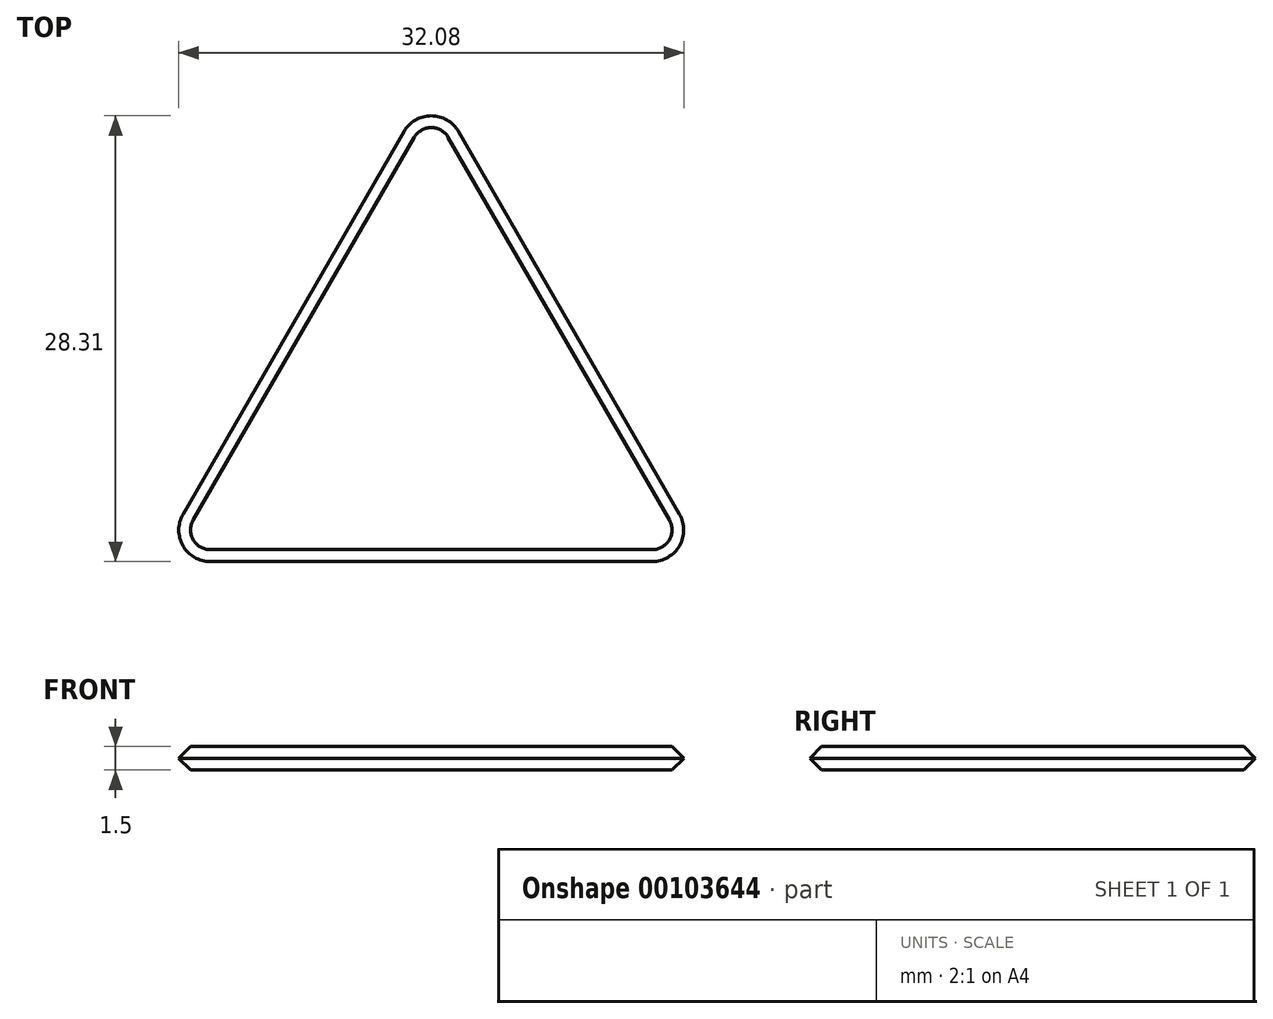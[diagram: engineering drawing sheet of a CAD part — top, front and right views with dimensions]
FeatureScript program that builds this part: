
annotation { "Feature Type Name" : "Feature", "Feature Type Description" : "" }
export const myFeature = defineFeature(function(context is Context, id is Id, definition is map)
    precondition{}
    {
        {
            var Q0;
            Q0=qCreatedBy(makeId("Top.planeOp"),FACE);
            var sketch = newSketch(context, id + "F0", { "sketchPlane" : qUnion([Q0])});
            skLineSegment(sketch, "E0", {"start": v(-1.73, 27.31) * mm, "end": v(-15.77, 3) * mm});
            skLineSegment(sketch, "E1", {"start": v(-14.04, 0) * mm, "end": v(14.04, 0) * mm});
            skLineSegment(sketch, "E2", {"start": v(15.77, 3) * mm, "end": v(1.73, 27.31) * mm});
            skPoint(sketch, "E3.visualSharp", {"position": v(0, 30.31) * mm});
            skArc(sketch, "E3.filletArc", {"start": v(1.73, 27.31) * mm, "mid": v(0, 28.31) * mm, "end": v(-1.73, 27.31) * mm});
            skPoint(sketch, "E4.visualSharp", {"position": v(17.5, 0) * mm});
            skArc(sketch, "E4.filletArc", {"start": v(14.04, 0) * mm, "mid": v(15.77, 1) * mm, "end": v(15.77, 3) * mm});
            skPoint(sketch, "E5.visualSharp", {"position": v(-17.5, 0) * mm});
            skArc(sketch, "E5.filletArc", {"start": v(-15.77, 3) * mm, "mid": v(-15.77, 1) * mm, "end": v(-14.04, 0) * mm});
            skSolve(sketch);
        }
        {
            var Q0;
            Q0=makeQuery(id+"F0.imprint","IMPRINT",FACE,{"disambiguationData":[TD([[makeQuery(id+"F0.imprint","IMPRINT",EDGE,{"derivedFrom":sQuery(id+"F0.wireOp",EDGE,"E0")}),1.0]])]});
            extrude(context, id + "F1", {"entities" : qUnion([Q0]), "endBound" : BoundingType.SYMMETRIC, "depth" : 1.5 * mm});
        }
        {
            var Q0;
            Q0=makeQuery(id+"F1.opExtrude","CAP_EDGE",EDGE,{"disambiguationData":[OSD([sQuery(id+"F0.wireOp",EDGE,"E2")])],"isStart":false});
            var Q1;
            Q1=makeQuery(id+"F1.opExtrude","CAP_EDGE",EDGE,{"disambiguationData":[OSD([sQuery(id+"F0.wireOp",EDGE,"E2")])],"isStart":true});
            var Q2;
            Q2=makeQuery(id+"F1.opExtrude","CAP_EDGE",EDGE,{"disambiguationData":[OSD([sQuery(id+"F0.wireOp",EDGE,"E1")])],"isStart":false});
            var Q3;
            Q3=makeQuery(id+"F1.opExtrude","CAP_EDGE",EDGE,{"disambiguationData":[OSD([sQuery(id+"F0.wireOp",EDGE,"E0")])],"isStart":false});
            var Q4;
            Q4=makeQuery(id+"F1.opExtrude","CAP_EDGE",EDGE,{"disambiguationData":[OSD([sQuery(id+"F0.wireOp",EDGE,"E1")])],"isStart":true});
            var Q5;
            Q5=makeQuery(id+"F1.opExtrude","CAP_EDGE",EDGE,{"disambiguationData":[OSD([sQuery(id+"F0.wireOp",EDGE,"E0")])],"isStart":true});
            chamfer(context, id + "F2", {"entities" : qUnion([Q0, Q1, Q2, Q3, Q4, Q5]), "width" : 0.75 * mm, "tangentPropagation" : true});
        }
    });
